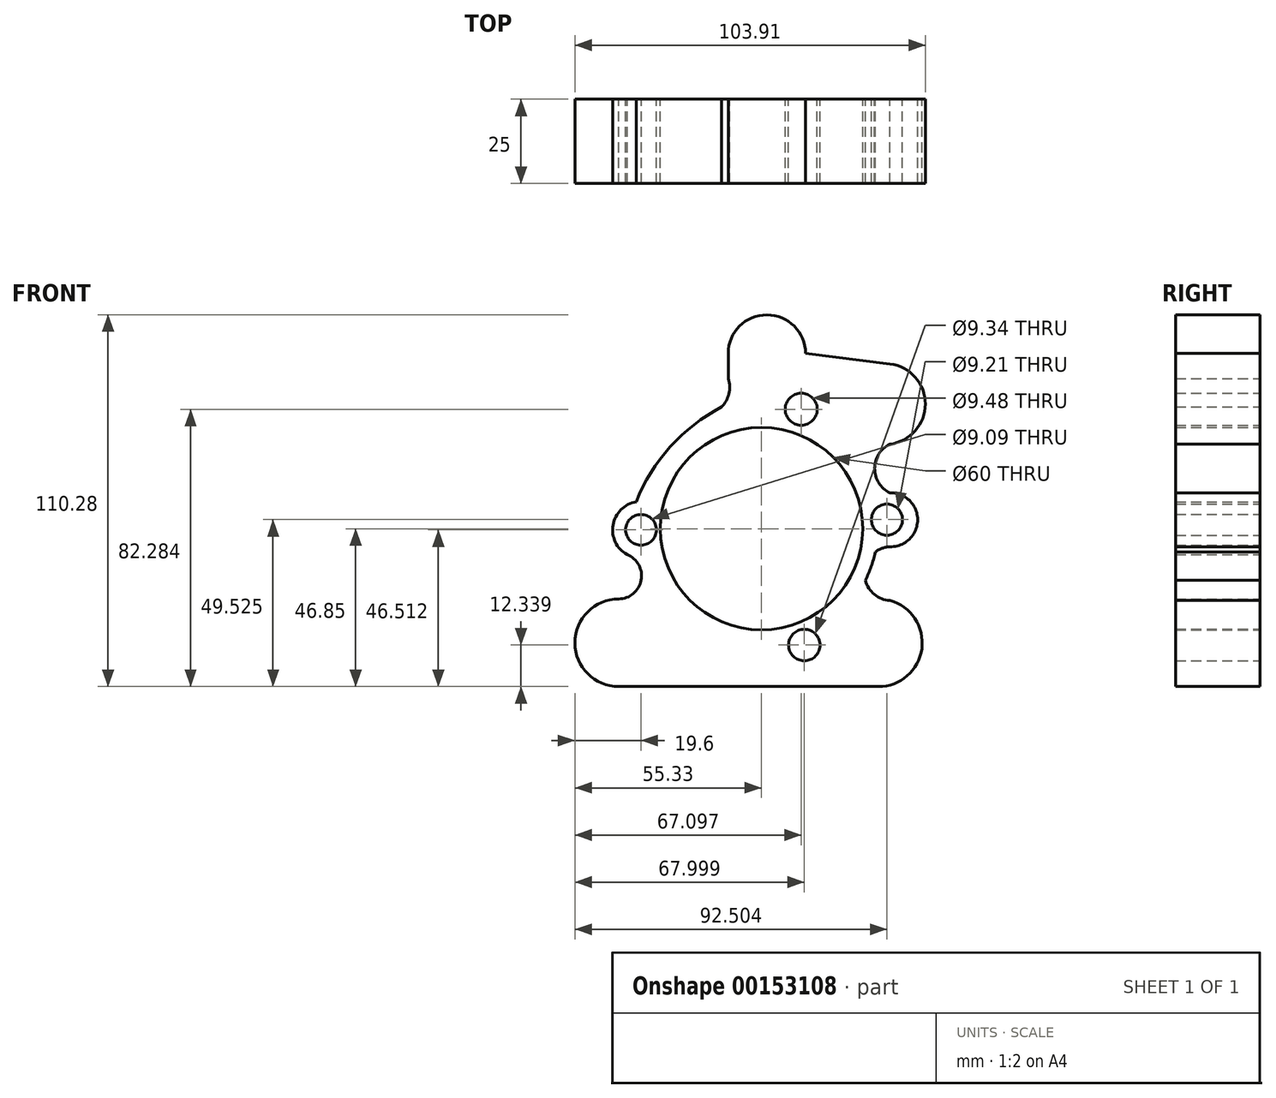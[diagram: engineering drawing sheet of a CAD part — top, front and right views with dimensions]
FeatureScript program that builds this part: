
annotation { "Feature Type Name" : "Feature", "Feature Type Description" : "" }
export const myFeature = defineFeature(function(context is Context, id is Id, definition is map)
    precondition{}
    {
        {
            var Q0;
            Q0=qCreatedBy(makeId("Front.planeOp"),FACE);
            var sketch = newSketch(context, id + "F0", { "sketchPlane" : qUnion([Q0])});
            skCircle(sketch, "E0", {"center": v(0, 0) * mm, "radius": 30 * mm});
            skArc(sketch, "E1", {"start": v(-11.91, 36.08) * mm, "mid": v(-9.68, 39.98) * mm, "end": v(-9.87, 44.47) * mm});
            skLineSegment(sketch, "E2", {"start": v(-9.87, 44.47) * mm, "end": v(-9.87, 51.98) * mm});
            skArc(sketch, "E3", {"start": v(13.04, 51.98) * mm, "mid": v(1.58, 63.43) * mm, "end": v(-9.87, 51.98) * mm});
            skLineSegment(sketch, "E4", {"start": v(13.04, 51.98) * mm, "end": v(38.06, 48.89) * mm});
            skArc(sketch, "E5", {"start": v(38.06, 25.07) * mm, "mid": v(48.58, 36.98) * mm, "end": v(38.06, 48.89) * mm});
            skArc(sketch, "E6", {"start": v(-42.33, -20.85) * mm, "mid": v(-55.33, -33.85) * mm, "end": v(-42.33, -46.85) * mm});
            skLineSegment(sketch, "E7", {"start": v(-42.33, -46.85) * mm, "end": v(34.64, -46.85) * mm});
            skArc(sketch, "E8", {"start": v(38.06, 25.07) * mm, "mid": v(33.53, 17.86) * mm, "end": v(38.06, 10.66) * mm});
            skArc(sketch, "E9", {"start": v(38.06, -5.34) * mm, "mid": v(46.27, 2.66) * mm, "end": v(38.06, 10.66) * mm});
            skArc(sketch, "E10", {"start": v(38.06, -5.34) * mm, "mid": v(30.52, -13.32) * mm, "end": v(38.06, -21.3) * mm});
            skArc(sketch, "E11", {"start": v(34.64, -46.85) * mm, "mid": v(47.52, -35.58) * mm, "end": v(38.06, -21.3) * mm});
            skCircle(sketch, "E12", {"center": v(-35.73, -0.34) * mm, "radius": 4.55 * mm});
            skArc(sketch, "E13", {"start": v(-37.16, 7.97) * mm, "mid": v(-44.04, 1.08) * mm, "end": v(-39.84, -7.7) * mm});
            skArc(sketch, "E14", {"start": v(-11.91, 36.08) * mm, "mid": v(-27.04, 24.28) * mm, "end": v(-37.16, 7.97) * mm});
            skArc(sketch, "E15", {"start": v(-42.33, -20.85) * mm, "mid": v(-35.7, -15.3) * mm, "end": v(-39.84, -7.7) * mm});
            skCircle(sketch, "E16", {"center": v(0, 0) * mm, "radius": 34.4 * mm});
            skCircle(sketch, "E17", {"center": v(12.67, -34.51) * mm, "radius": 4.67 * mm});
            skCircle(sketch, "E18", {"center": v(37.17, 2.68) * mm, "radius": 4.6 * mm});
            skCircle(sketch, "E19", {"center": v(11.77, 35.43) * mm, "radius": 4.74 * mm});
            skSolve(sketch);
        }
        {
            var Q0;
            Q0 = qSketchRegion(id + "F0", true);
            var Q1;
            Q1=makeQuery(id+"F0.imprint","IMPRINT",FACE,{"disambiguationData":[TD([[makeQuery(id+"F0.imprint","IMPRINT",EDGE,{"derivedFrom":sQuery(id+"F0.wireOp",EDGE,"E1")}),-1.0]])]});
            extrude(context, id + "F1", {"entities" : qUnion([Q0, Q1]), "depth" : 25 * mm});
        }
    });
